# Revit family: Vario-DP_přímý_DN015_RFA_2018
name_source: partatom
category: Pipe Accessories
revit_build: Autodesk Revit LT 2018 (Build: 20180329_1100(x64)
units: mm (PartAtom-declared; Revit-internal decimal feet)

## family parameters
Always vertical = Yes
Cut with Voids When Loaded = No
Part Type = Valve - Breaks Into
Round Connector Dimension = Use Diameter
Shared = No
Work Plane-Based = No

## types (3) — shared parameters
BBVIS = No
BZ = 48 mm  [stored 0.15748 ft]
CAT = No
CAT0 = Yes
CenSd_RT0X_6 = 7 mm  [stored 0.0229659 ft]
DS1 = 15 mm  [stored 0.0492126 ft]
DS2 = 9 mm  [stored 0.0295276 ft]
DS3 = 4 mm  [stored 0.0131234 ft]
ENBL350 = No
H = 23 mm  [stored 0.0754593 ft]
HS = 16 mm  [stored 0.0524934 ft]
L1 = 8 mm  [stored 0.0262467 ft]
L1__ve = -8 mm  [stored -0.0262467 ft]
L2 = 10 mm  [stored 0.0328084 ft]
L22 = 13 mm  [stored 0.0426509 ft]
L22__ve = -13 mm  [stored -0.0426509 ft]
L2D_Min = 30 mm  [stored 0.0984252 ft]
LLDAndHLD = Yes
LLDONLY = Yes
MC Enable LOD 200 = No
MC Enable LOD 350 = No
MC Pressure Drop Maximum Value = 0.0 Pa
MC Pressure Drop Minimum Value = 0.0 Pa
MC Use Limits From Balancing Method = No
Manufacturer = Hydronix
QmdConnectorList = 301;D;302;D
RR = 5 mm  [stored 0.0164042 ft]
RT0 = 10 mm  [stored 0.0328084 ft]
RT00 = 6 mm  [stored 0.019685 ft]
RT01 = 9 mm  [stored 0.0295276 ft]
RT0X = 9 mm  [stored 0.0295276 ft]
RT2 = 11 mm  [stored 0.0360892 ft]
RT_0 = 9 mm  [stored 0.0295276 ft]
RT_01 = 8 mm  [stored 0.0262467 ft]
SW = Yes
SW1 = Yes
SW11 = No
SW1_ENBL350 = No
SW1_LLDONLY = Yes
SW2 = No
SW22 = No
SW2_ENBL350 = No
SW2_LLDAndHLD = No
SW2_LLDONLY = No
SW_1 = Yes
SW_2 = No
Type Comments = Termostatický radiátorový ventil s integrovaným omezovačem průtoku; přímý; závitový, PN10; +0~+90°C; pracovní dp 15-70kPa; max. síla pohonu 120N; připojení hlavice: M30x1,5
URL = www.hydronix.cz
VIS0 = No
magiPartTypeId = 303
magiProductFamilyId = 9a3b6d3dc30f4d82b1fd8b50564aa5
zero-valued in all types: MC Throttling Maximum Value, MC Throttling Minimum Value

## per-type parameters (varying)
- Vario-DP přímý DN10: BY=16 mm  [stored 0.0524934 ft]; C=32 mm  [stored 0.104987 ft]; CenSd_RT1_6=12 mm  [stored 0.0393701 ft]; CenSd_RT22_6=12 mm  [stored 0.0393701 ft]; D=10 mm; DT=17 mm  [stored 0.0557743 ft]; Description=Termostatický radiátorový ventil s omezovačem max. průtoku; DN10; rozsah nastavení omezovače max. průtok: 20-340l/h; L=75 mm; L2D=75 mm; LP=8 mm  [stored 0.0262467 ft]; LT=85 mm  [stored 0.278871 ft]; L_=75 mm; L_2=38 mm; MC Product Code=VARIO-DP; přímý DN10; (obj.č.: 161010100); dpmin=15kPa; dpmax: 70kPa;; rozsah nastavení 20-340l/h; RT=8 mm  [stored 0.0262467 ft]; RT02=12 mm  [stored 0.0393701 ft]; RT1=13 mm  [stored 0.0426509 ft]; RT22=14 mm  [stored 0.0459318 ft]; RT4=9 mm  [stored 0.0295276 ft]; RTX=1 mm  [stored 0.00328084 ft]; RT_1=11 mm  [stored 0.0360892 ft]; TL=10 mm  [stored 0.0328084 ft]; TL__ve=-10 mm  [stored -0.0328084 ft]; W2D=10 mm  [stored 0.0328084 ft]; Z1=4 mm  [stored 0.0131234 ft]; magiProductId=cff3df26e6cf48da84c7a4aeae022f
- Vario-DP přímý DN20: BY=19 mm  [stored 0.062336 ft]; C=40 mm; CenSd_RT1_6=16 mm  [stored 0.0524934 ft]; CenSd_RT22_6=17 mm  [stored 0.0557743 ft]; D=20 mm; DT=26 mm; Description=Termostatický radiátorový ventil s omezovačem max. průtoku; DN20; rozsah nastavení omezovače max. průtok: 20-340l/h; L=92 mm; L2D=92 mm; LP=9 mm  [stored 0.0295276 ft]; LT=106 mm; L_=92 mm; L_2=46 mm; MC Product Code=VARIO-DP; přímý DN20; (obj.č.: 161030100); dpmin=15kPa; dpmax: 70kPa;; rozsah nastavení 20-340l/h; RT=13 mm  [stored 0.0426509 ft]; RT02=16 mm  [stored 0.0524934 ft]; RT1=18 mm  [stored 0.0590551 ft]; RT22=19 mm  [stored 0.062336 ft]; RT4=14 mm  [stored 0.0459318 ft]; RTX=6 mm  [stored 0.019685 ft]; RT_1=16 mm  [stored 0.0524934 ft]; TL=15 mm  [stored 0.0492126 ft]; TL__ve=-15 mm  [stored -0.0492126 ft]; W2D=20 mm  [stored 0.0656168 ft]; Z1=7 mm  [stored 0.0229659 ft]; magiProductId=65e4e24176f04ec8add0c08a0806a3
- Vario-DP přímý DN15: BY=16 mm  [stored 0.0524934 ft]; C=36 mm  [stored 0.11811 ft]; CenSd_RT1_6=13 mm  [stored 0.0426509 ft]; CenSd_RT22_6=14 mm  [stored 0.0459318 ft]; D=15 mm; DT=21 mm  [stored 0.0688976 ft]; Description=Termostatický radiátorový ventil s omezovačem max. průtoku; DN15; rozsah nastavení omezovače max. průtok: 20-340l/h; L=82 mm; L2D=82 mm; LP=8 mm  [stored 0.0262467 ft]; LT=95 mm; L_=82 mm; L_2=41 mm; MC Product Code=VARIO-DP; přímý DN15; (obj.č.: 161020100); dpmin=15kPa; dpmax: 70kPa;; rozsah nastavení 20-340l/h; RT=11 mm  [stored 0.0360892 ft]; RT02=15 mm  [stored 0.0492126 ft]; RT1=16 mm  [stored 0.0524934 ft]; RT22=17 mm  [stored 0.0557743 ft]; RT4=11 mm  [stored 0.0360892 ft]; RTX=4 mm  [stored 0.0131234 ft]; RT_1=14 mm  [stored 0.0459318 ft]; TL=13 mm  [stored 0.0426509 ft]; TL__ve=-13 mm  [stored -0.0426509 ft]; W2D=15 mm  [stored 0.0492126 ft]; Z1=5 mm  [stored 0.0164042 ft]; magiProductId=86c7649ae082497d8c558b15a6d69e

note: [stored X ft] marks values corroborated as IEEE doubles in the binary element streams (Revit-internal decimal feet)

## geometry (parser evidence)
native form markers: Sweep x16
no freeform markers — native parametric forms only
